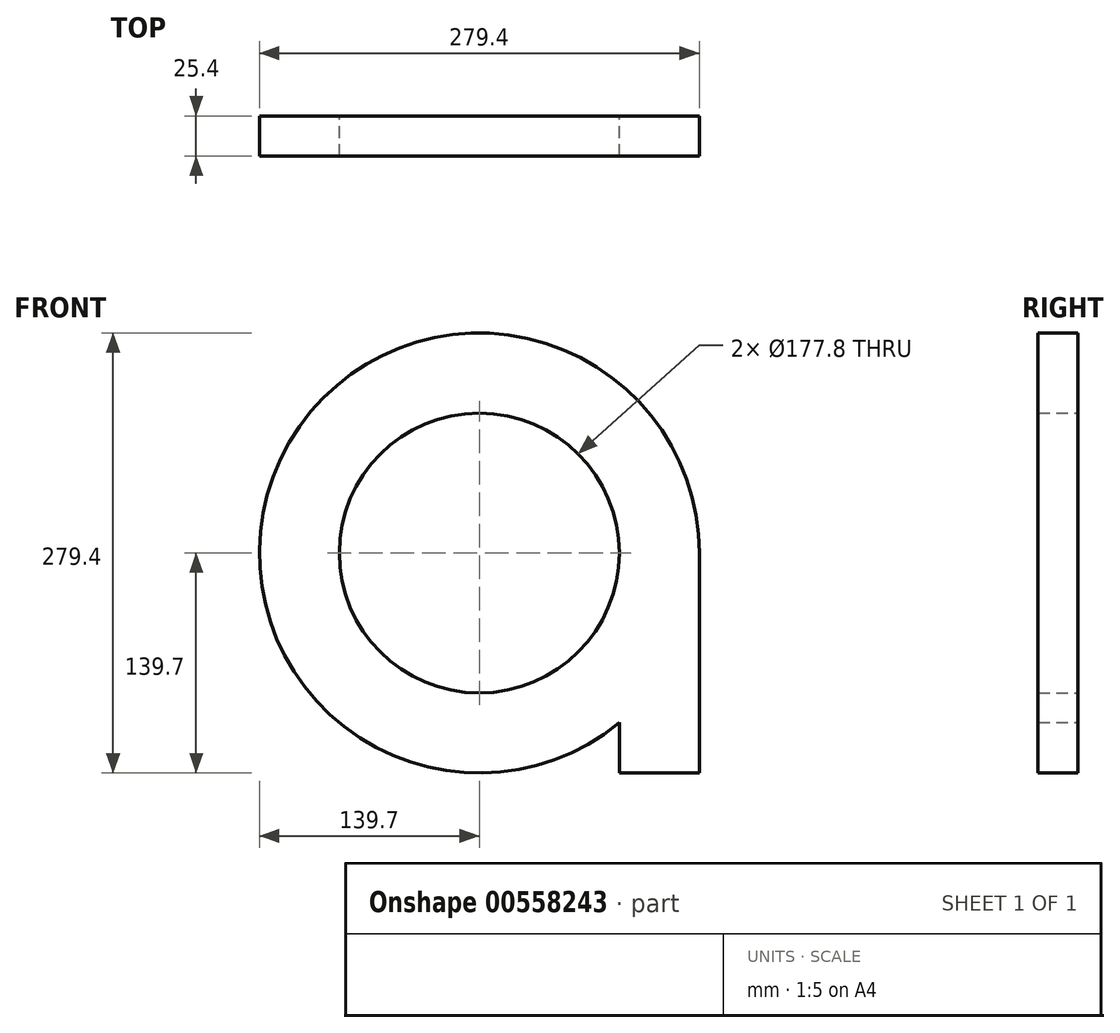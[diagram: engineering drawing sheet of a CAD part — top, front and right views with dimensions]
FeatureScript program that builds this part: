
annotation { "Feature Type Name" : "Feature", "Feature Type Description" : "" }
export const myFeature = defineFeature(function(context is Context, id is Id, definition is map)
    precondition{}
    {
        {
            var Q0;
            Q0=qCreatedBy(makeId("Front.planeOp"),FACE);
            var sketch = newSketch(context, id + "F0", { "sketchPlane" : qUnion([Q0])});
            skArc(sketch, "E0", {"start": v(139.7, 0) * mm, "mid": v(-126.36, 59.57) * mm, "end": v(88.9, -107.76) * mm});
            skCircle(sketch, "E1", {"center": v(0, 0) * mm, "radius": 88.9 * mm});
            skLineSegment(sketch, "E2", {"start": v(139.7, 0) * mm, "end": v(139.7, -139.7) * mm});
            skLineSegment(sketch, "E3", {"start": v(139.7, -139.7) * mm, "end": v(88.9, -139.7) * mm});
            skLineSegment(sketch, "E4", {"start": v(88.9, -139.7) * mm, "end": v(88.9, -107.76) * mm});
            skSolve(sketch);
        }
        {
            var Q0;
            Q0 = qSketchRegion(id + "F0", true);
            extrude(context, id + "F1", {"entities" : qUnion([Q0]), "depth" : 25.4 * mm, "offsetDistance" : 25.4 * mm});
        }
    });
